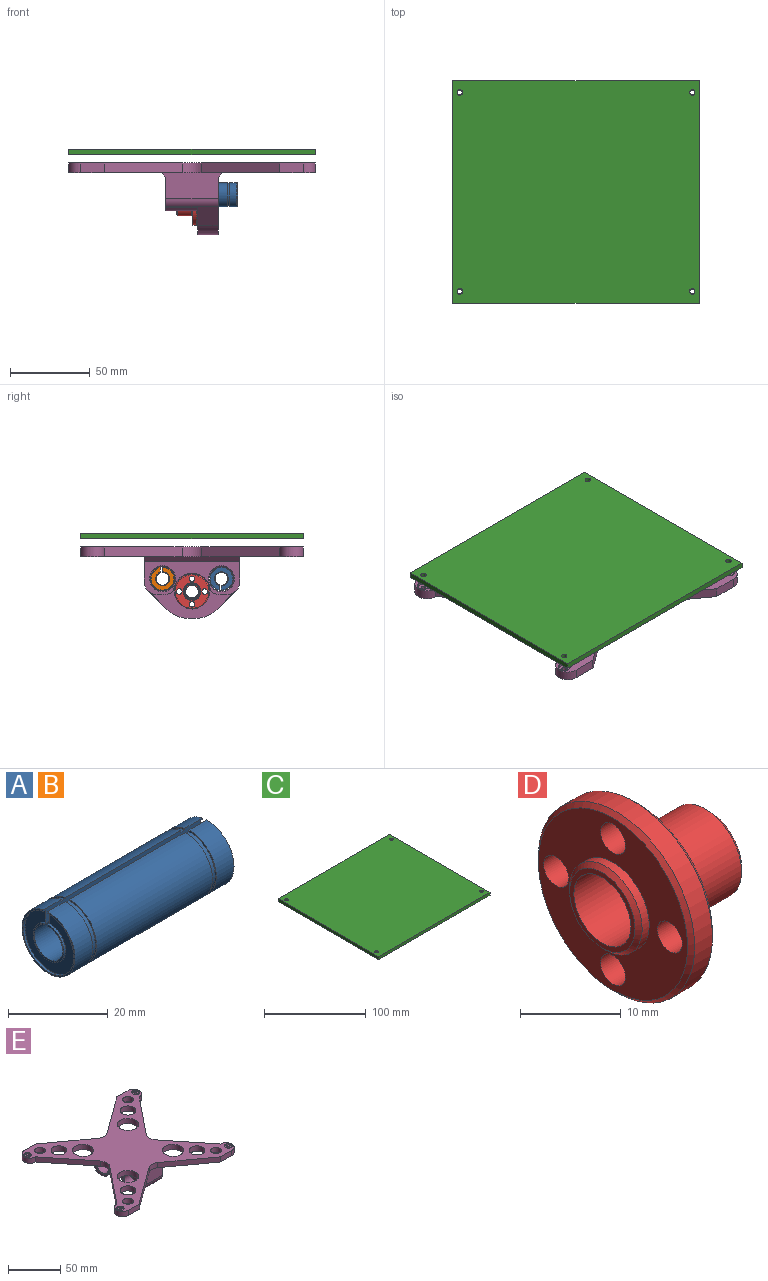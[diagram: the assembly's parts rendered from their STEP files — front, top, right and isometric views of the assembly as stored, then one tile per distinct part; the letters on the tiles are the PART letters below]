
ASSEMBLY  parts=5 mates=4
PART A: 22 faces, bbox 45x15x15 mm
  f0: plane 8.7x8.7mm, normal (-1,0,0), area 8.8mm2, adj f4,f17,f20,f21
  f1: plane 8.7x8.7mm, normal (1,0,0), area 8.8mm2, adj f4,f14,f20,f21
  f2: cylinder r=7.5mm len=32.8mm, axis (-1,0,0), area 1507.4mm2, adj f8,f11,f20,f21
  f3: cylinder r=7.5mm len=15mm, axis (-1,0,0), area 229.8mm2, adj f7,f9,f20,f21
  f4: cylinder r=4mm len=45mm, axis (-1,0,0), area 1077.5mm2, adj f0,f1,f20,f21
  f5: cylinder r=7.5mm len=15mm, axis (-1,0,0), area 229.8mm2, adj f6,f12,f20,f21
  f6: plane 15x15mm, normal (1,0,0), area 15.7mm2, adj f5,f15,f20,f21
  f7: plane 15x15mm, normal (-1,0,0), area 15.7mm2, adj f3,f18,f20,f21
  f8: plane 15x15mm, normal (-1,0,0), area 15.7mm2, adj f2,f10,f20,f21
  f9: plane 15x15mm, normal (1,0,0), area 15.7mm2, adj f3,f10,f20,f21
  f10: cylinder r=7.15mm len=14.3mm, axis (-1,0,0), area 48.1mm2, adj f8,f9,f20,f21
  f11: plane 15x15mm, normal (1,0,0), area 15.7mm2, adj f2,f13,f20,f21
  f12: plane 15x15mm, normal (-1,0,0), area 15.7mm2, adj f5,f13,f20,f21
  f13: cylinder r=7.15mm len=14.3mm, axis (1,0,0), area 48.1mm2, adj f11,f12,f20,f21
  f14: cylinder r=4.35mm len=8.7mm, axis (1,0,0), area 13.1mm2, adj f1,f16,f20,f21
  f15: cylinder r=7.15mm len=14.3mm, axis (1,0,0), area 21.9mm2, adj f6,f16,f20,f21
  f16: plane 14.3x14.3mm, normal (1,0,0), area 97.9mm2, adj f14,f15,f20,f21
  f17: cylinder r=4.35mm len=8.7mm, axis (-1,0,0), area 13.1mm2, adj f0,f19,f20,f21
  f18: cylinder r=7.15mm len=14.3mm, axis (-1,0,0), area 21.9mm2, adj f7,f19,f20,f21
  f19: plane 14.3x14.3mm, normal (-1,0,0), area 97.9mm2, adj f17,f18,f20,f21
  f20: plane 45x3.62mm, normal (0,-1,0), area 159.4mm2, adj f0,f1,f2,f3,f4,f5,f6,f7
  f21: plane 45x3.5mm, normal (0,1,0), area 154.1mm2, adj f0,f1,f2,f3,f4,f5,f6,f7
PART B: same geometry as A
PART C: 10 faces, bbox 155x140x3.5 mm
  f0: plane 155x140mm, normal (0,0,1), area 21661.5mm2, adj f2,f3,f4,f5,f6,f7,f8,f9
  f1: plane 155x140mm, normal (0,0,-1), area 21661.5mm2, adj f2,f3,f4,f5,f6,f7,f8,f9
  f2: plane 140x3.5mm, normal (1,0,0), area 490mm2, adj f0,f1,f3,f5
  f3: plane 155x3.5mm, normal (0,1,0), area 542.5mm2, adj f0,f1,f2,f4
  f4: plane 140x3.5mm, normal (-1,0,0), area 490mm2, adj f0,f1,f3,f5
  f5: plane 155x3.5mm, normal (0,-1,0), area 542.5mm2, adj f0,f1,f2,f4
  f6: cylinder r=1.75mm len=3.5mm, axis (0,0,1), area 38.5mm2, adj f0,f1
  f7: cylinder r=1.75mm len=3.5mm, axis (0,0,1), area 38.5mm2, adj f0,f1
  f8: cylinder r=1.75mm len=3.5mm, axis (0,0,1), area 38.5mm2, adj f0,f1
  f9: cylinder r=1.75mm len=3.5mm, axis (0,0,1), area 38.5mm2, adj f0,f1
PART D: 17 faces, bbox 15x22x22 mm
  f0: cylinder r=11mm len=22mm, axis (-1,0,0), area 172.8mm2, adj f10,f11
  f1: plane 21x21mm, normal (1,0,0), area 209.4mm2, adj f8,f11,f13,f14,f15,f16
  f2: plane 21x21mm, normal (-1,0,0), area 226.2mm2, adj f6,f10,f13,f14,f15,f16
  f3: cylinder r=5.1mm len=10.2mm, axis (-1,0,0), area 288.4mm2, adj f8,f12
  f4: plane 9.2x9.2mm, normal (1,0,0), area 16.2mm2, adj f5,f12
  f5: cylinder r=4mm len=15mm, axis (1,0,0), area 377mm2, adj f4,f7
  f6: cylinder r=5.1mm len=10.2mm, axis (1,0,0), area 32mm2, adj f2,f9
  f7: plane 9.2x9.2mm, normal (-1,0,0), area 16.2mm2, adj f5,f9
  f8: cone r=5.1mm half-angle=45deg, axis (-1,0,0), area 23.8mm2, adj f1,f3
  f9: cone r=4.6mm half-angle=45deg, axis (1,0,0), area 21.5mm2, adj f6,f7
  f10: cone r=11mm half-angle=45deg, axis (1,0,0), area 47.8mm2, adj f0,f2
  f11: cone r=10.5mm half-angle=45deg, axis (-1,0,0), area 47.8mm2, adj f0,f1
  f12: cone r=4.6mm half-angle=45deg, axis (-1,0,0), area 21.5mm2, adj f3,f4
  f13: cylinder r=1.75mm len=3.5mm, axis (1,0,0), area 38.5mm2, adj f1,f2
  f14: cylinder r=1.75mm len=3.5mm, axis (1,0,0), area 38.5mm2, adj f1,f2
  f15: cylinder r=1.75mm len=3.5mm, axis (1,0,0), area 38.5mm2, adj f1,f2
  f16: cylinder r=1.75mm len=3.5mm, axis (1,0,0), area 38.5mm2, adj f1,f2
PART E: 83 faces, bbox 155x140x45 mm
  f0: plane 60x21.18mm, normal (-1,0,0), area 548.7mm2, adj f1,f2,f5,f6,f19,f20,f21,f25
  f1: plane 38.8x16.1mm, normal (0,-1,0), area 537.1mm2, adj f0,f3,f34,f35,f81,f82
  f2: plane 38.8x16.1mm, normal (0,1,0), area 537.1mm2, adj f0,f3,f33,f35,f81,f82
  f3: plane 60x36mm, normal (1,0,0), area 1172.9mm2, adj f1,f2,f4,f5,f6,f7,f8,f14
  f4: plane 12.8x3.43mm, normal (0,0,-1), area 43.9mm2, adj f3,f7,f8,f13
  f5: plane 32.8x12.09mm, normal (0,-0.71,-0.71), area 249.2mm2, adj f0,f3,f7,f13,f32,f34
  f6: plane 32.8x12.09mm, normal (0,0.71,-0.71), area 249.1mm2, adj f0,f3,f8,f13,f31,f33
  f7: cylinder r=20mm len=14.14mm, axis (1,0,0), area 201.1mm2, adj f3,f4,f5,f13
  f8: cylinder r=20mm len=14.14mm, axis (1,0,0), area 201.1mm2, adj f3,f4,f6,f13
  f9: cylinder r=7.68mm len=31.8mm, axis (1,0,0), area 1533.5mm2, adj f20,f23
  f10: cylinder r=5.4mm len=11.8mm, axis (1,0,0), area 400.4mm2, adj f18,f24
  f11: cylinder r=7.68mm len=31.8mm, axis (1,0,0), area 1533.5mm2, adj f21,f22
  f12: cylinder r=11mm len=21.11mm, axis (-1,0,0), area 551.3mm2, adj f13,f19,f29,f30
  f13: plane 53.76x28mm, normal (-1,0,0), area 608.4mm2, adj f4,f5,f6,f7,f8,f12,f14,f15
  f14: cylinder r=1.75mm len=12.8mm, axis (-1,0,0), area 140.7mm2, adj f3,f13
  f15: cylinder r=1.75mm len=12.8mm, axis (-1,0,0), area 140.7mm2, adj f3,f13
  f16: cylinder r=1.75mm len=12.8mm, axis (-1,0,0), area 140.7mm2, adj f3,f13
  f17: cylinder r=1.75mm len=12.8mm, axis (-1,0,0), area 140.7mm2, adj f3,f13
  f18: cone r=5.4mm half-angle=45deg, axis (-1,0,0), area 25.1mm2, adj f10,f13
  f19: cone r=11mm half-angle=45deg, axis (-1,0,0), area 22.4mm2, adj f0,f12,f29,f30
  f20: cone r=7.68mm half-angle=45deg, axis (-1,0,0), area 35.2mm2, adj f0,f9
  f21: cone r=7.68mm half-angle=45deg, axis (-1,0,0), area 35.2mm2, adj f0,f11
  f22: cone r=7.68mm half-angle=45deg, axis (1,0,0), area 35.2mm2, adj f3,f11
  f23: cone r=7.68mm half-angle=45deg, axis (1,0,0), area 35.2mm2, adj f3,f9
  f24: cone r=5.4mm half-angle=45deg, axis (1,0,0), area 25.1mm2, adj f3,f10
  f25: cylinder r=10.18mm len=20mm, axis (-1,0,0), area 89mm2, adj f0,f13,f26,f30
  f26: plane 20x3.03mm, normal (0,0,-1), area 60.6mm2, adj f0,f13,f25,f31
  f27: cylinder r=10.18mm len=20mm, axis (-1,0,0), area 85.3mm2, adj f0,f13,f28,f29
  f28: plane 20x3.21mm, normal (0,0,-1), area 64.2mm2, adj f0,f13,f27,f32
  f29: cylinder r=7mm len=20mm, axis (1,0,0), area 123.5mm2, adj f0,f12,f13,f19,f27
  f30: cylinder r=7mm len=20mm, axis (1,0,0), area 123.5mm2, adj f0,f12,f13,f19,f25
  f31: cylinder r=7mm len=20mm, axis (-1,0,0), area 110mm2, adj f0,f6,f13,f26
  f32: cylinder r=7mm len=20mm, axis (-1,0,0), area 110mm2, adj f0,f5,f13,f28
  f33: cylinder r=7mm len=32.8mm, axis (-1,0,0), area 180.3mm2, adj f0,f2,f3,f6
  f34: cylinder r=7mm len=32.8mm, axis (1,0,0), area 180.3mm2, adj f0,f1,f3,f5
  f35: plane 155x140mm, normal (0,0,-1), area 6124.2mm2, adj f1,f2,f37,f40,f43,f46,f48,f49
  f36: plane 7.5x7.5mm, normal (0,0,1), area 37.1mm2, adj f37,f38
  f37: cylinder r=1.5mm len=4.5mm, axis (0,0,1), area 42.4mm2, adj f35,f36
  f38: cylinder r=3.75mm len=7.5mm, axis (0,0,1), area 35.3mm2, adj f36,f79
  f39: plane 7.5x7.5mm, normal (0,0,1), area 37.1mm2, adj f40,f41
  f40: cylinder r=1.5mm len=4.5mm, axis (0,0,1), area 42.4mm2, adj f35,f39
  f41: cylinder r=3.75mm len=7.5mm, axis (0,0,1), area 35.3mm2, adj f39,f79
  f42: plane 7.5x7.5mm, normal (0,0,1), area 37.1mm2, adj f43,f44
  f43: cylinder r=1.5mm len=4.5mm, axis (0,0,1), area 42.4mm2, adj f35,f42
  f44: cylinder r=3.75mm len=7.5mm, axis (0,0,1), area 35.3mm2, adj f42,f79
  f45: plane 7.5x7.5mm, normal (0,0,1), area 37.1mm2, adj f46,f47
  f46: cylinder r=1.5mm len=4.5mm, axis (0,0,1), area 42.4mm2, adj f35,f45
  f47: cylinder r=3.75mm len=7.5mm, axis (0,0,1), area 35.3mm2, adj f45,f79
  f48: cylinder r=5mm len=10mm, axis (0,0,-1), area 188.5mm2, adj f35,f79
  f49: cylinder r=10mm len=20mm, axis (0,0,-1), area 377mm2, adj f35,f79
  f50: cylinder r=7.5mm len=15mm, axis (0,0,-1), area 282.7mm2, adj f35,f79
  f51: cylinder r=10mm len=20mm, axis (0,0,-1), area 377mm2, adj f35,f79
  f52: cylinder r=7.5mm len=15mm, axis (0,0,-1), area 282.7mm2, adj f35,f79
  f53: cylinder r=7.5mm len=15mm, axis (0,0,1), area 141.4mm2, adj f35,f54,f72,f79
  f54: plane 15x6mm, normal (0,-1,0), area 90mm2, adj f35,f53,f55,f79
  f55: plane 49.12x35.72mm, normal (0.59,-0.81,0), area 364.4mm2, adj f35,f54,f56,f79
  f56: cylinder r=10mm len=11.76mm, axis (0,0,1), area 75.5mm2, adj f35,f55,f57,f79
  f57: plane 49.12x35.72mm, normal (-0.59,-0.81,0), area 364.4mm2, adj f35,f56,f58,f79
  f58: plane 15x6mm, normal (0,-1,0), area 90mm2, adj f35,f57,f59,f79
  f59: cylinder r=7.5mm len=15mm, axis (0,0,1), area 141.4mm2, adj f35,f58,f60,f79
  f60: plane 48.75x39mm, normal (0.78,0.62,0), area 374.6mm2, adj f35,f59,f61,f79
  f61: cylinder r=10mm len=12.49mm, axis (0,0,1), area 81mm2, adj f35,f60,f62,f79
  f62: plane 48.75x39mm, normal (0.78,-0.62,0), area 374.6mm2, adj f35,f61,f63,f79
  f63: cylinder r=7.5mm len=15mm, axis (0,0,1), area 141.4mm2, adj f35,f62,f64,f79
  f64: plane 15x6mm, normal (0,1,0), area 90mm2, adj f35,f63,f65,f79
  f65: plane 49.12x35.72mm, normal (-0.59,0.81,0), area 364.4mm2, adj f35,f64,f66,f79
  f66: cylinder r=10mm len=11.76mm, axis (0,0,1), area 75.5mm2, adj f35,f65,f67,f79
  f67: plane 49.12x35.72mm, normal (0.59,0.81,0), area 364.4mm2, adj f35,f66,f68,f79
  f68: plane 15x6mm, normal (0,1,0), area 90mm2, adj f35,f67,f69,f79
  f69: cylinder r=7.5mm len=15mm, axis (0,0,1), area 141.4mm2, adj f35,f68,f70,f79
  f70: plane 48.75x39mm, normal (-0.78,-0.62,0), area 374.6mm2, adj f35,f69,f71,f79
  f71: cylinder r=10mm len=12.49mm, axis (0,0,1), area 81mm2, adj f35,f70,f72,f79
  f72: plane 48.75x39mm, normal (-0.78,0.62,0), area 374.6mm2, adj f35,f53,f71,f79
  f73: cylinder r=10mm len=20mm, axis (0,0,-1), area 377mm2, adj f35,f79
  f74: cylinder r=10mm len=20mm, axis (0,0,-1), area 377mm2, adj f35,f79
  f75: cylinder r=7.5mm len=15mm, axis (0,0,-1), area 282.7mm2, adj f35,f79
  f76: cylinder r=5mm len=10mm, axis (0,0,-1), area 188.5mm2, adj f35,f79
  f77: cylinder r=7.5mm len=15mm, axis (0,0,-1), area 282.7mm2, adj f35,f79
  f78: cylinder r=5mm len=10mm, axis (0,0,-1), area 188.5mm2, adj f35,f79
  f79: plane 155x140mm, normal (0,0,1), area 8303.8mm2, adj f38,f41,f44,f47,f48,f49,f50,f51
  f80: cylinder r=5mm len=10mm, axis (0,0,-1), area 188.5mm2, adj f35,f79
  f81: plane 60x3mm, normal (0.71,0,-0.71), area 254.6mm2, adj f1,f2,f3,f35
  f82: plane 60x3mm, normal (-0.71,0,-0.71), area 254.6mm2, adj f0,f1,f2,f35
PLACE A rot(axis=(0,1,0),180deg) t=(6.1,-18.5,25)mm
PLACE B t=(6.1,18.5,25)mm
PLACE C t=(0,0,50)mm
PLACE D rot(axis=(0,0,-1),180deg) t=(3.6,0,17)mm
PLACE E at identity fixed
MATE fastened A.f2 <-> E.f9  axis (-1,0,0) through (-16.4,-18.5,25)mm
MATE fastened C.f6 <-> E.f37  axis (0,0,-1) through (-73,62.5,50)mm
MATE fastened E.f21 <-> B.f2  axis (-1,0,0) through (-16.4,18.5,25)mm
MATE fastened D.f16 <-> E.f14  axis (1,0,0) through (3.6,0,25)mm
